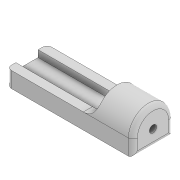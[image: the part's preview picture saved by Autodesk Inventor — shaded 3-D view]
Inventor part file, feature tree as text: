
AUTODESK INVENTOR PART (.ipt)
format: ipt  version: 2022 (Build 260153000, 153)  size: 147,968 bytes
history: native  units: mm
features: extrude x3, fillet x3, sketch x3, projected_geometry x1
ambient origin geometry x8: Origin, YZ Plane, XZ Plane, XY Plane, X Axis, Y Axis, Z Axis, Center Point
bodies: Solid1 (feature_tree)
feature tree (10):
  extrude  "Extrusion1"  Depth=2.0mm
  extrude  "Extrusion2"  Depth=2.0mm
  extrude  "Extrusion3"  Depth=1.5mm
  fillet  "Fillet1"  Radius=20.0mm
  fillet  "Fillet2"  Radius=8.0mm
  fillet  "Fillet3"  Radius=1.6mm
  sketch  "Sketch1"  dims[d0=2.0mm d1=2.0mm]
  sketch  "Sketch2"  dims[d2=2.0mm d4=2.475mm]
  projected_geometry  "Projected Loop1"
  sketch  "Sketch3"  dims[d5=2.475mm d6=1.5mm d7=20.0mm d8=0.0mm d9=8.0mm d10=0.0mm d11=1.6mm d12=10.0mm d13=0.0mm d14=3.0mm d15=1.0mm d16=1.0mm d17=1.5mm]
